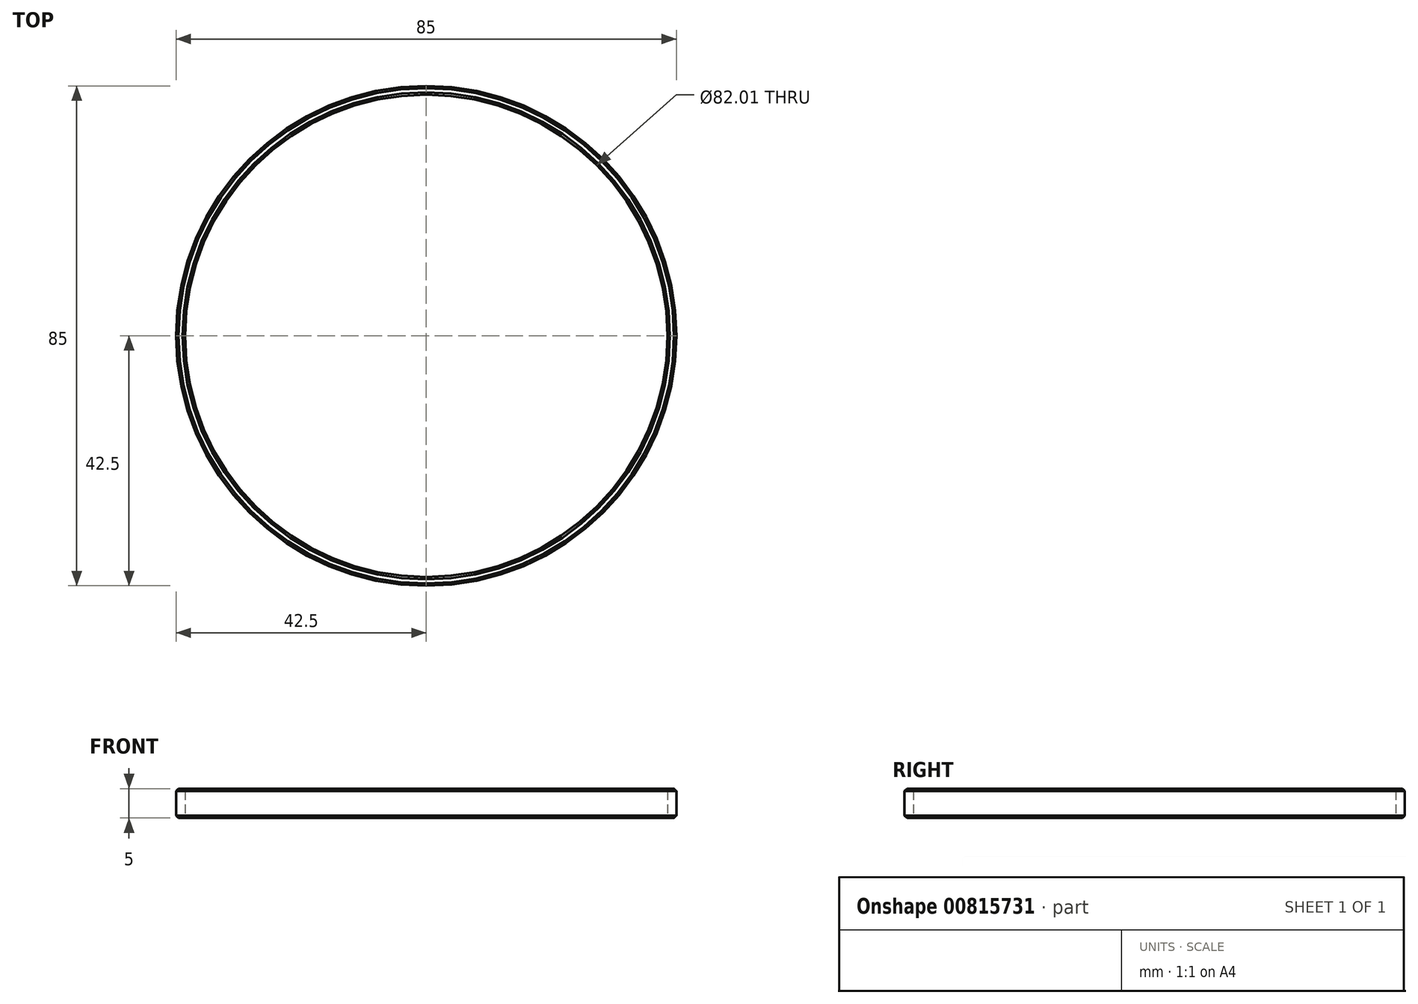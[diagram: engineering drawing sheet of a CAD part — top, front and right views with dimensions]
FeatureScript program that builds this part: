
annotation { "Feature Type Name" : "Feature", "Feature Type Description" : "" }
export const myFeature = defineFeature(function(context is Context, id is Id, definition is map)
    precondition{}
    {
        {
            var Q0;
            Q0=qCreatedBy(makeId("Top.planeOp"),FACE);
            var sketch = newSketch(context, id + "F0", { "sketchPlane" : qUnion([Q0])});
            skCircle(sketch, "E0", {"center": v(0, 0) * mm, "radius": 42.5 * mm});
            skCircle(sketch, "E1", {"center": v(0, 0) * mm, "radius": 41 * mm});
            skSolve(sketch);
        }
        {
            var Q0;
            Q0=makeQuery(id+"F0.imprint","IMPRINT",FACE,{"disambiguationData":[TD([[makeQuery(id+"F0.imprint","IMPRINT",EDGE,{"derivedFrom":sQuery(id+"F0.wireOp",EDGE,"E0")}),1.0]])]});
            extrude(context, id + "F1", {"entities" : qUnion([Q0]), "depth" : 5 * mm, "offsetDistance" : 25 * mm});
        }
        {
            var Q0;
            Q0=makeQuery(id+"F1.opExtrude","CAP_EDGE",EDGE,{"disambiguationData":[OSD([sQuery(id+"F0.wireOp",EDGE,"E0")])],"isStart":false});
            var Q1;
            Q1=makeQuery(id+"F1.opExtrude","CAP_EDGE",EDGE,{"disambiguationData":[OSD([sQuery(id+"F0.wireOp",EDGE,"E0")])],"isStart":true});
            chamfer(context, id + "F2", {"entities" : qUnion([Q0, Q1]), "width" : .4 * mm, "tangentPropagation" : true});
        }
        {
            var Q0;
            Q0=makeQuery(id+"F1.opExtrude","CAP_EDGE",EDGE,{"disambiguationData":[OSD([sQuery(id+"F0.wireOp",EDGE,"E1")])],"isStart":false});
            var Q1;
            Q1=makeQuery(id+"F1.opExtrude","CAP_EDGE",EDGE,{"disambiguationData":[OSD([sQuery(id+"F0.wireOp",EDGE,"E1")])],"isStart":true});
            chamfer(context, id + "F3", {"entities" : qUnion([Q0, Q1]), "width" : .4 * mm, "tangentPropagation" : true});
        }
    });
